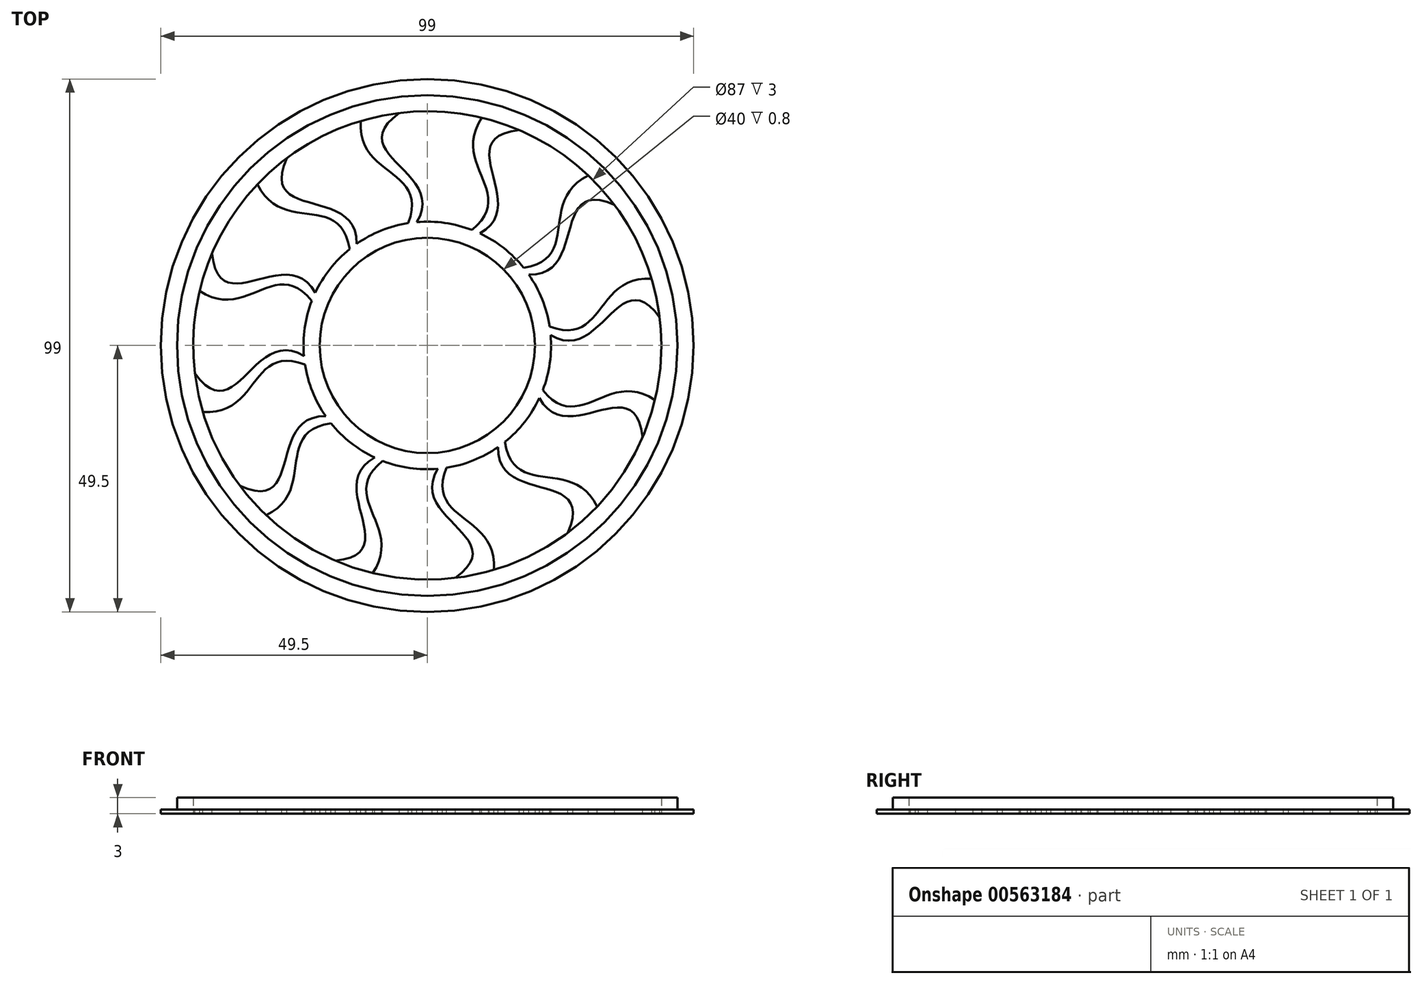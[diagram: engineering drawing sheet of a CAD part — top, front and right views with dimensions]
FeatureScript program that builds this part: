
annotation { "Feature Type Name" : "Feature", "Feature Type Description" : "" }
export const myFeature = defineFeature(function(context is Context, id is Id, definition is map)
    precondition{}
    {
        {
            assignVariable(context, id + "F0", {"name" : "T", "anyValue" : 0.8});
        }
        {
            assignVariable(context, id + "F1", {"name" : "E", "anyValue" : 3});
        }
        {
            var Q0;
            Q0=qCreatedBy(makeId("Top.planeOp"),FACE);
            var sketch = newSketch(context, id + "F2", { "sketchPlane" : qUnion([Q0])});
            skCircle(sketch, "E0", {"center": v(0, 0) * mm, "radius": 20 * mm});
            skCircle(sketch, "E1", {"center": v(0, 0) * mm, "radius": 43.5 * mm});
            skCircle(sketch, "E2", {"center": v(0, 0) * mm, "radius": 46.5 * mm});
            skCircle(sketch, "E3", {"center": v(0, 0) * mm, "radius": 49.5 * mm});
            skSolve(sketch);
        }
        {
            var Q0;
            Q0=makeQuery(id+"F2.imprint","IMPRINT",FACE,{"disambiguationData":[TD([[makeQuery(id+"F2.imprint","IMPRINT",EDGE,{"derivedFrom":sQuery(id+"F2.wireOp",EDGE,"E1")}),-1.0]])]});
            extrude(context, id + "F3", {"entities" : qUnion([Q0]), "depth" : getVariable(context, 'E') * mm, "offsetDistance" : 25 * mm});
        }
        {
            var Q0;
            Q0=makeQuery(id+"F2.imprint","IMPRINT",FACE,{"disambiguationData":[TD([[makeQuery(id+"F2.imprint","IMPRINT",EDGE,{"derivedFrom":sQuery(id+"F2.wireOp",EDGE,"E0")}),-1.0]])]});
            var Q1;
            Q1=makeQuery(id+"F2.imprint","IMPRINT",FACE,{"disambiguationData":[TD([[makeQuery(id+"F2.imprint","IMPRINT",EDGE,{"derivedFrom":sQuery(id+"F2.wireOp",EDGE,"E2")}),-1.0]])]});
            extrude(context, id + "F4", {"entities" : qUnion([Q0, Q1]), "operationType" : NewBodyOperationType.ADD, "depth" : getVariable(context, 'T') * mm, "offsetDistance" : 25 * mm});
        }
        {
            var Q0;
            Q0=makeQuery(id+"F4.opExtrude","CAP_FACE",FACE,{"disambiguationData":[OSD([sQuery(id+"F2.wireOp",EDGE,"E0"),sQuery(id+"F2.wireOp",EDGE,"E1")])],"isStart":false});
            var sketch = newSketch(context, id + "F5", { "sketchPlane" : qUnion([Q0])});
            skCircle(sketch, "E4", {"center": v(0, 0) * mm, "radius": 23 * mm});
            skCircle(sketch, "E5.0", {"center": v(0, 0) * mm, "radius": 43.5 * mm});
            skFitSpline(sketch, "E6", {"points": [v(5.2, -43.19) * mm, v(1.95, -22.92) * mm], "startDerivative": vector(32.05, 23.12) * mm, "endDerivative": vector(17.11, 28.1) * mm});
            skFitSpline(sketch, "E7", {"points": [v(-10.14, -42.3) * mm, v(-8.3, -21.45) * mm], "startDerivative": vector(17.62, 26.34) * mm, "endDerivative": vector(25.43, 20.74) * mm});
            skLineSegment(sketch, "E8", {"start": v(-8.3, -21.45) * mm, "end": v(0, 0) * mm, "construction": true});
            skLineSegment(sketch, "E9", {"start": v(1.95, -22.92) * mm, "end": v(0, 0) * mm, "construction": true});
            skLineSegment(sketch, "E10", {"start": v(0, 0) * mm, "end": v(5.2, -43.19) * mm, "construction": true});
            skSolve(sketch);
        }
        {
            var Q0;
            {var subQ0=sQuery(id+"F5.wireOp",EDGE,"E6");Q0=makeQuery(id+"F5.imprint","IMPRINT",FACE,{"disambiguationData":[TD([[makeQuery(id+"F5.imprint","IMPRINT",EDGE,{"derivedFrom":subQ0}),1.0]])]});}
            extrude(context, id + "F6", {"entities" : qUnion([Q0]), "oppositeDirection" : true, "depth" : 2 * getVariable(context, 'T') * mm, "offsetDistance" : 25 * mm, "symmetric" : true});
        }
        {
            var Q0;
            Q0=qCreatedBy(makeId("Front.planeOp"),FACE);
            var sketch = newSketch(context, id + "F7", { "sketchPlane" : qUnion([Q0])});
            skLineSegment(sketch, "E11", {"start": v(0, 0) * mm, "end": v(0, 24.12) * mm, "construction": true});
            skSolve(sketch);
        }
        {
            var Q0;
            Q0=makeQuery(id+"F6.opExtrude","SWEPT_BODY",BODY,{"disambiguationData":[OSD([sQuery(id+"F5.wireOp",EDGE,"E4"),sQuery(id+"F5.wireOp",EDGE,"E5.0"),sQuery(id+"F5.wireOp",EDGE,"E6"),sQuery(id+"F5.wireOp",EDGE,"E7")])]});
            var Q1;
            Q1=sQuery(id+"F7.wireOp",EDGE,"E11");
            circularPattern(context, id + "F8", {"entities" : qUnion([Q0]), "axis" : qUnion([Q1]), "angle" : 360 * degree, "instanceCount" : 12, "equalSpace" : true});
        }
        {
            var Q0;
            Q0=makeQuery(id+"F6.opExtrude","SWEPT_BODY",BODY,{"disambiguationData":[OSD([sQuery(id+"F5.wireOp",EDGE,"E4"),sQuery(id+"F5.wireOp",EDGE,"E5.0"),sQuery(id+"F5.wireOp",EDGE,"E6"),sQuery(id+"F5.wireOp",EDGE,"E7")])]});
            var Q1;
            Q1=makeQuery(id+"F8.opPattern","COPY",BODY,{"derivedFrom":makeQuery(id+"F6.opExtrude","SWEPT_BODY",BODY,{"disambiguationData":[OSD([sQuery(id+"F5.wireOp",EDGE,"E4"),sQuery(id+"F5.wireOp",EDGE,"E5.0"),sQuery(id+"F5.wireOp",EDGE,"E6"),sQuery(id+"F5.wireOp",EDGE,"E7")])]}),"instanceName":"1"});
            var Q2;
            Q2=makeQuery(id+"F8.opPattern","COPY",BODY,{"derivedFrom":makeQuery(id+"F6.opExtrude","SWEPT_BODY",BODY,{"disambiguationData":[OSD([sQuery(id+"F5.wireOp",EDGE,"E4"),sQuery(id+"F5.wireOp",EDGE,"E5.0"),sQuery(id+"F5.wireOp",EDGE,"E6"),sQuery(id+"F5.wireOp",EDGE,"E7")])]}),"instanceName":"2"});
            var Q3;
            Q3=makeQuery(id+"F8.opPattern","COPY",BODY,{"derivedFrom":makeQuery(id+"F6.opExtrude","SWEPT_BODY",BODY,{"disambiguationData":[OSD([sQuery(id+"F5.wireOp",EDGE,"E4"),sQuery(id+"F5.wireOp",EDGE,"E5.0"),sQuery(id+"F5.wireOp",EDGE,"E6"),sQuery(id+"F5.wireOp",EDGE,"E7")])]}),"instanceName":"3"});
            var Q4;
            Q4=makeQuery(id+"F8.opPattern","COPY",BODY,{"derivedFrom":makeQuery(id+"F6.opExtrude","SWEPT_BODY",BODY,{"disambiguationData":[OSD([sQuery(id+"F5.wireOp",EDGE,"E4"),sQuery(id+"F5.wireOp",EDGE,"E5.0"),sQuery(id+"F5.wireOp",EDGE,"E6"),sQuery(id+"F5.wireOp",EDGE,"E7")])]}),"instanceName":"4"});
            var Q5;
            Q5=makeQuery(id+"F8.opPattern","COPY",BODY,{"derivedFrom":makeQuery(id+"F6.opExtrude","SWEPT_BODY",BODY,{"disambiguationData":[OSD([sQuery(id+"F5.wireOp",EDGE,"E4"),sQuery(id+"F5.wireOp",EDGE,"E5.0"),sQuery(id+"F5.wireOp",EDGE,"E6"),sQuery(id+"F5.wireOp",EDGE,"E7")])]}),"instanceName":"5"});
            var Q6;
            Q6=makeQuery(id+"F8.opPattern","COPY",BODY,{"derivedFrom":makeQuery(id+"F6.opExtrude","SWEPT_BODY",BODY,{"disambiguationData":[OSD([sQuery(id+"F5.wireOp",EDGE,"E4"),sQuery(id+"F5.wireOp",EDGE,"E5.0"),sQuery(id+"F5.wireOp",EDGE,"E6"),sQuery(id+"F5.wireOp",EDGE,"E7")])]}),"instanceName":"6"});
            var Q7;
            Q7=makeQuery(id+"F8.opPattern","COPY",BODY,{"derivedFrom":makeQuery(id+"F6.opExtrude","SWEPT_BODY",BODY,{"disambiguationData":[OSD([sQuery(id+"F5.wireOp",EDGE,"E4"),sQuery(id+"F5.wireOp",EDGE,"E5.0"),sQuery(id+"F5.wireOp",EDGE,"E6"),sQuery(id+"F5.wireOp",EDGE,"E7")])]}),"instanceName":"7"});
            var Q8;
            Q8=makeQuery(id+"F8.opPattern","COPY",BODY,{"derivedFrom":makeQuery(id+"F6.opExtrude","SWEPT_BODY",BODY,{"disambiguationData":[OSD([sQuery(id+"F5.wireOp",EDGE,"E4"),sQuery(id+"F5.wireOp",EDGE,"E5.0"),sQuery(id+"F5.wireOp",EDGE,"E6"),sQuery(id+"F5.wireOp",EDGE,"E7")])]}),"instanceName":"8"});
            var Q9;
            Q9=makeQuery(id+"F8.opPattern","COPY",BODY,{"derivedFrom":makeQuery(id+"F6.opExtrude","SWEPT_BODY",BODY,{"disambiguationData":[OSD([sQuery(id+"F5.wireOp",EDGE,"E4"),sQuery(id+"F5.wireOp",EDGE,"E5.0"),sQuery(id+"F5.wireOp",EDGE,"E6"),sQuery(id+"F5.wireOp",EDGE,"E7")])]}),"instanceName":"9"});
            var Q10;
            Q10=makeQuery(id+"F8.opPattern","COPY",BODY,{"derivedFrom":makeQuery(id+"F6.opExtrude","SWEPT_BODY",BODY,{"disambiguationData":[OSD([sQuery(id+"F5.wireOp",EDGE,"E4"),sQuery(id+"F5.wireOp",EDGE,"E5.0"),sQuery(id+"F5.wireOp",EDGE,"E6"),sQuery(id+"F5.wireOp",EDGE,"E7")])]}),"instanceName":"10"});
            var Q11;
            Q11=makeQuery(id+"F8.opPattern","COPY",BODY,{"derivedFrom":makeQuery(id+"F6.opExtrude","SWEPT_BODY",BODY,{"disambiguationData":[OSD([sQuery(id+"F5.wireOp",EDGE,"E4"),sQuery(id+"F5.wireOp",EDGE,"E5.0"),sQuery(id+"F5.wireOp",EDGE,"E6"),sQuery(id+"F5.wireOp",EDGE,"E7")])]}),"instanceName":"11"});
            var Q12;
            Q12=makeQuery(id+"F3.opExtrude","SWEPT_BODY",BODY,{"disambiguationData":[OSD([sQuery(id+"F2.wireOp",EDGE,"E1"),sQuery(id+"F2.wireOp",EDGE,"E2")])]});
            booleanBodies(context, id + "F9", {"operationType" : BooleanOperationType.SUBTRACTION, "tools" : qUnion([Q0, Q1, Q2, Q3, Q4, Q5, Q6, Q7, Q8, Q9, Q10, Q11]), "targets" : qUnion([Q12])});
        }
    });
